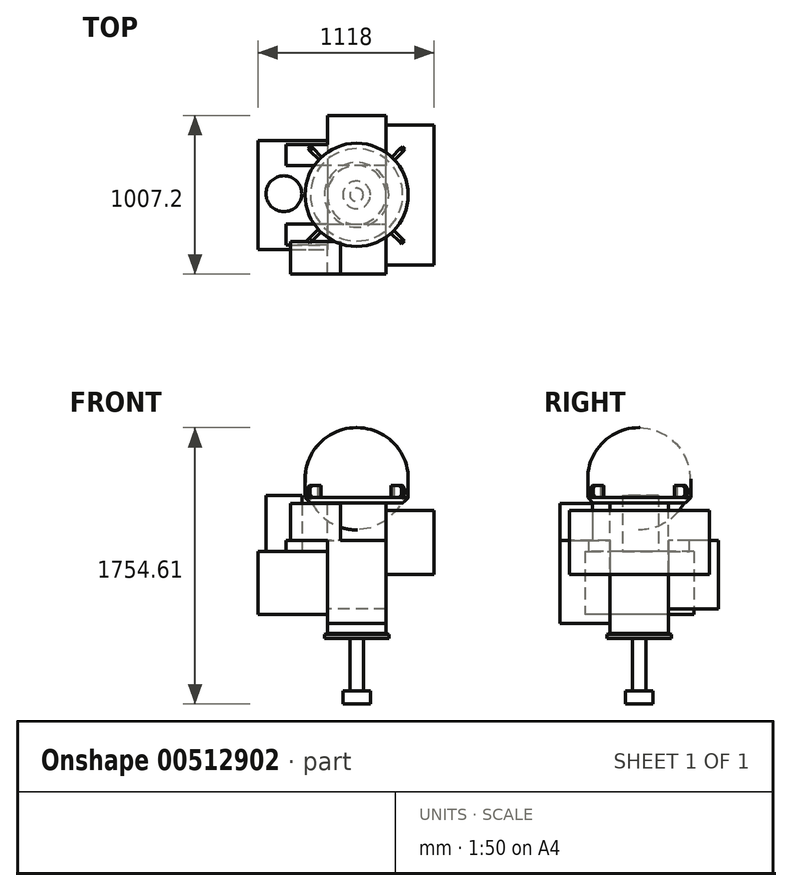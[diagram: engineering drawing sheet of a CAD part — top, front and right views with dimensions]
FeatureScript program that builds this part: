
annotation { "Feature Type Name" : "Feature", "Feature Type Description" : "" }
export const myFeature = defineFeature(function(context is Context, id is Id, definition is map)
    precondition{}
    {
        {
            var Q0;
            Q0=qCreatedBy(makeId("Front.planeOp"),FACE);
            var sketch = newSketch(context, id + "F0", { "sketchPlane" : qUnion([Q0])});
            skLineSegment(sketch, "E0", {"start": v(0, 0) * mm, "end": v(0, 25.3) * mm});
            skLineSegment(sketch, "E1", {"start": v(0, 25.3) * mm, "end": v(-18.9, 29.6) * mm});
            skLineSegment(sketch, "E2", {"start": v(-18.9, 29.6) * mm, "end": v(-18.9, 858.7) * mm});
            skLineSegment(sketch, "E3", {"start": v(-18.9, 858.7) * mm, "end": v(122.8, 858.7) * mm});
            skLineSegment(sketch, "E4", {"start": v(122.8, 858.7) * mm, "end": v(122.8, 1013) * mm});
            skLineSegment(sketch, "E5", {"start": v(-205, 1405.57) * mm, "end": v(-205, 307.85) * mm, "construction": true});
            skLineSegment(sketch, "E6", {"start": v(0, 0) * mm, "end": v(-205, 0) * mm});
            skPoint(sketch, "E7", {"position": v(-205, 1338) * mm});
            skArc(sketch, "E8", {"start": v(122.8, 1013) * mm, "mid": v(26.62, 1243.8) * mm, "end": v(-205, 1338) * mm});
            skLineSegment(sketch, "E9", {"start": v(-205, 1338) * mm, "end": v(-205, 0) * mm});
            skSolve(sketch);
        }
        {
            var Q0;
            Q0=makeQuery(id+"F0.imprint","IMPRINT",FACE,{"disambiguationData":[TD([[makeQuery(id+"F0.imprint","IMPRINT",EDGE,{"derivedFrom":sQuery(id+"F0.wireOp",EDGE,"E0")}),1.0]])]});
            var Q1;
            Q1=sQuery(id+"F0.wireOp",EDGE,"E5");
            revolve(context, id + "F1", {"entities" : qUnion([Q0]), "axis" : qUnion([Q1]), "revolveType" : RevolveType.FULL});
        }
        {
            var Q0;
            Q0=makeQuery(id+"F1.opRevolve","SWEPT_EDGE",EDGE,{"disambiguationData":[OSD([sQuery(id+"F0.wireOp",EDGE,"E3"),sQuery(id+"F0.wireOp",EDGE,"E4")])]});
            chamfer(context, id + "F2", {"entities" : qUnion([Q0]), "width" : 35 * mm, "tangentPropagation" : true});
        }
        {
            var Q0;
            Q0=makeQuery(id+"F1.opRevolve","SWEPT_EDGE",EDGE,{"disambiguationData":[OSD([sQuery(id+"F0.wireOp",EDGE,"E2"),sQuery(id+"F0.wireOp",EDGE,"E3")])]});
            fillet(context, id + "F3", {"entities" : qUnion([Q0]), "radius" : 8 * mm, "tangentPropagation" : true, "allowEdgeOverflow" : false});
        }
        {
            var Q0;
            Q0=makeQuery(id+"F1.opRevolve","SWEPT_FACE",FACE,{"disambiguationData":[OSD([sQuery(id+"F0.wireOp",EDGE,"E6")])]});
            var sketch = newSketch(context, id + "F4", { "sketchPlane" : qUnion([Q0])});
            skCircle(sketch, "E10", {"center": v(-205, 0) * mm, "radius": 42.3 * mm});
            skSolve(sketch);
        }
        {
            var Q0;
            Q0=makeQuery(id+"F4.imprint","IMPRINT",FACE,{"disambiguationData":[TD([[makeQuery(id+"F4.imprint","IMPRINT",EDGE,{"derivedFrom":sQuery(id+"F4.wireOp",EDGE,"E10")}),1.0]])]});
            extrude(context, id + "F5", {"entities" : qUnion([Q0]), "operationType" : NewBodyOperationType.ADD, "depth" : 416.6 * mm});
        }
        {
            var Q0;
            Q0=qCreatedBy(makeId("Right.planeOp"),FACE);
            cPlane(context, id + "F6", {"entities" : qUnion([Q0]), "cplaneType" : CPlaneType.OFFSET, "offset" : 18.9 * mm, "oppositeDirection" : true, "width" : 150 * mm, "height" : 150 * mm});
        }
        {
            var Q0;
            Q0=qCreatedBy(id+"F6.planeOp",FACE);
            var sketch = newSketch(context, id + "F7", { "sketchPlane" : qUnion([Q0])});
            skLineSegment(sketch, "E11.bottom", {"start": v(-445, 811.6) * mm, "end": v(445, 811.6) * mm});
            skLineSegment(sketch, "E11.top", {"start": v(-445, 405.8) * mm, "end": v(445, 405.8) * mm});
            skLineSegment(sketch, "E11.left", {"start": v(-445, 811.6) * mm, "end": v(-445, 405.8) * mm});
            skLineSegment(sketch, "E11.right", {"start": v(445, 811.6) * mm, "end": v(445, 405.8) * mm});
            skSolve(sketch);
        }
        {
            var Q0;
            Q0=qSketchRegion(id+"F7",true);
            extrude(context, id + "F8", {"entities" : qUnion([Q0]), "operationType" : NewBodyOperationType.ADD, "depth" : 305.8 * mm});
        }
        {
            var Q0;
            Q0=qCreatedBy(id+"F6.planeOp",FACE);
            cPlane(context, id + "F9", {"entities" : qUnion([Q0]), "cplaneType" : CPlaneType.OFFSET, "offset" : 372.2 * mm, "oppositeDirection" : true, "width" : 150 * mm, "height" : 150 * mm});
        }
        {
            var Q0;
            Q0=qCreatedBy(id+"F9.planeOp",FACE);
            var sketch = newSketch(context, id + "F10", { "sketchPlane" : qUnion([Q0])});
            skLineSegment(sketch, "E12.bottom", {"start": v(346, 552.3) * mm, "end": v(-346, 552.3) * mm});
            skLineSegment(sketch, "E12.top", {"start": v(346, 150.6) * mm, "end": v(-346, 150.6) * mm});
            skLineSegment(sketch, "E12.left", {"start": v(346, 552.3) * mm, "end": v(346, 150.6) * mm});
            skLineSegment(sketch, "E12.right", {"start": v(-346, 552.3) * mm, "end": v(-346, 150.6) * mm});
            skSolve(sketch);
        }
        {
            var Q0;
            Q0=qSketchRegion(id+"F10",true);
            extrude(context, id + "F11", {"entities" : qUnion([Q0]), "operationType" : NewBodyOperationType.ADD, "oppositeDirection" : true, "depth" : 440 * mm});
        }
        {
            var Q0;
            Q0=makeQuery(id+"F11.opExtrude","SWEPT_FACE",FACE,{"disambiguationData":[OSD([sQuery(id+"F10.wireOp",EDGE,"E12.bottom")])]});
            var sketch = newSketch(context, id + "F12", { "sketchPlane" : qUnion([Q0])});
            skCircle(sketch, "E13", {"center": v(-667.1, 7.5) * mm, "radius": 114 * mm});
            skSolve(sketch);
        }
        {
            var Q0;
            Q0=qSketchRegion(id+"F12",true);
            extrude(context, id + "F13", {"entities" : qUnion([Q0]), "operationType" : NewBodyOperationType.ADD, "depth" : 356.5 * mm});
        }
        {
            var Q0;
            Q0=qCreatedBy(makeId("Front.planeOp"),FACE);
            cPlane(context, id + "F14", {"entities" : qUnion([Q0]), "cplaneType" : CPlaneType.OFFSET, "offset" : 186.1 * mm, "width" : 150 * mm, "height" : 150 * mm});
        }
        {
            var Q0;
            Q0=qCreatedBy(id+"F14.planeOp",FACE);
            var sketch = newSketch(context, id + "F15", { "sketchPlane" : qUnion([Q0])});
            skLineSegment(sketch, "E14.bottom", {"start": v(-391.1, 622.7) * mm, "end": v(-18.9, 622.7) * mm});
            skLineSegment(sketch, "E14.top", {"start": v(-391.1, 94.5) * mm, "end": v(-18.9, 94.5) * mm});
            skLineSegment(sketch, "E14.left", {"start": v(-391.1, 622.7) * mm, "end": v(-391.1, 94.5) * mm});
            skLineSegment(sketch, "E14.right", {"start": v(-18.9, 622.7) * mm, "end": v(-18.9, 94.5) * mm});
            skSolve(sketch);
        }
        {
            var Q0;
            Q0=qSketchRegion(id+"F15",true);
            extrude(context, id + "F16", {"entities" : qUnion([Q0]), "depth" : 317.5 * mm});
        }
        {
            var Q0;
            Q0=qCreatedBy(makeId("Front.planeOp"),FACE);
            cPlane(context, id + "F17", {"entities" : qUnion([Q0]), "cplaneType" : CPlaneType.OFFSET, "offset" : 186.1 * mm, "oppositeDirection" : true, "width" : 150 * mm, "height" : 150 * mm});
        }
        {
            var Q0;
            Q0=qCreatedBy(id+"F17.planeOp",FACE);
            var sketch = newSketch(context, id + "F18", { "sketchPlane" : qUnion([Q0])});
            skLineSegment(sketch, "E15.bottom", {"start": v(-18.9, 621) * mm, "end": v(-391.1, 621) * mm});
            skLineSegment(sketch, "E15.top", {"start": v(-18.9, 186.6) * mm, "end": v(-391.1, 186.6) * mm});
            skLineSegment(sketch, "E15.left", {"start": v(-18.9, 621) * mm, "end": v(-18.9, 186.6) * mm});
            skLineSegment(sketch, "E15.right", {"start": v(-391.1, 621) * mm, "end": v(-391.1, 186.6) * mm});
            skSolve(sketch);
        }
        {
            var Q0;
            Q0=qSketchRegion(id+"F18",true);
            extrude(context, id + "F19", {"entities" : qUnion([Q0]), "oppositeDirection" : true, "depth" : 317.5 * mm});
        }
        {
            var Q0;
            Q0=makeQuery(id+"F16.opExtrude","SWEPT_FACE",FACE,{"disambiguationData":[OSD([sQuery(id+"F15.wireOp",EDGE,"E14.bottom")])]});
            var sketch = newSketch(context, id + "F20", { "sketchPlane" : qUnion([Q0])});
            skLineSegment(sketch, "E16.bottom", {"start": v(-626, -297.6) * mm, "end": v(-308.5, -297.6) * mm});
            skLineSegment(sketch, "E16.top", {"start": v(-626, -503.6) * mm, "end": v(-308.5, -503.6) * mm});
            skLineSegment(sketch, "E16.left", {"start": v(-626, -297.6) * mm, "end": v(-626, -503.6) * mm});
            skLineSegment(sketch, "E16.right", {"start": v(-308.5, -297.6) * mm, "end": v(-308.5, -503.6) * mm});
            skSolve(sketch);
        }
        {
            var Q0;
            Q0=qSketchRegion(id+"F20",true);
            extrude(context, id + "F21", {"entities" : qUnion([Q0]), "depth" : 234 * mm});
        }
        {
            var Q0;
            Q0=makeQuery(id+"F19.opExtrude","SWEPT_FACE",FACE,{"disambiguationData":[OSD([sQuery(id+"F18.wireOp",EDGE,"E15.bottom")])]});
            var sketch = newSketch(context, id + "F22", { "sketchPlane" : qUnion([Q0])});
            skLineSegment(sketch, "E17.bottom", {"start": v(-652.9, 318.2) * mm, "end": v(-391.1, 318.2) * mm});
            skLineSegment(sketch, "E17.top", {"start": v(-652.9, 186.1) * mm, "end": v(-391.1, 186.1) * mm});
            skLineSegment(sketch, "E17.left", {"start": v(-652.9, 318.2) * mm, "end": v(-652.9, 186.1) * mm});
            skLineSegment(sketch, "E17.right", {"start": v(-391.1, 318.2) * mm, "end": v(-391.1, 186.1) * mm});
            skSolve(sketch);
        }
        {
            var Q0;
            Q0=qSketchRegion(id+"F22",true);
            extrude(context, id + "F23", {"entities" : qUnion([Q0]), "operationType" : NewBodyOperationType.ADD, "endBound" : BoundingType.UP_TO_NEXT, "oppositeDirection" : true, "depth" : 25 * mm});
        }
        {
            var Q0;
            Q0=makeQuery(id+"F16.opExtrude","SWEPT_FACE",FACE,{"disambiguationData":[OSD([sQuery(id+"F15.wireOp",EDGE,"E14.bottom")])]});
            var sketch = newSketch(context, id + "F24", { "sketchPlane" : qUnion([Q0])});
            skLineSegment(sketch, "E18.bottom", {"start": v(-652.9, -186.1) * mm, "end": v(-391.1, -186.1) * mm});
            skLineSegment(sketch, "E18.top", {"start": v(-652.9, -318.2) * mm, "end": v(-391.1, -318.2) * mm});
            skLineSegment(sketch, "E18.left", {"start": v(-652.9, -186.1) * mm, "end": v(-652.9, -318.2) * mm});
            skLineSegment(sketch, "E18.right", {"start": v(-391.1, -186.1) * mm, "end": v(-391.1, -318.2) * mm});
            skSolve(sketch);
        }
        {
            var Q0;
            Q0=qSketchRegion(id+"F24",true);
            extrude(context, id + "F25", {"entities" : qUnion([Q0]), "operationType" : NewBodyOperationType.ADD, "endBound" : BoundingType.UP_TO_NEXT, "oppositeDirection" : true, "depth" : 25 * mm});
        }
        {
            var Q0;
            Q0=makeQuery(id+"F5.opExtrude","CAP_FACE",FACE,{"disambiguationData":[OSD([sQuery(id+"F4.wireOp",EDGE,"E10")])],"isStart":false});
            var sketch = newSketch(context, id + "F26", { "sketchPlane" : qUnion([Q0])});
            skCircle(sketch, "E19", {"center": v(-205, 0) * mm, "radius": 87.5 * mm});
            skSolve(sketch);
        }
        {
            var Q0;
            Q0 = qSketchRegion(id + "F26", true);
            extrude(context, id + "F27", {"entities" : qUnion([Q0]), "operationType" : NewBodyOperationType.ADD, "oppositeDirection" : true, "depth" : 83 * mm});
        }
        {
            var Q0;
            Q0=makeQuery(id+"F1.opRevolve","SWEPT_FACE",FACE,{"disambiguationData":[OSD([sQuery(id+"F0.wireOp",EDGE,"E3")])]});
            cPlane(context, id + "F28", {"entities" : qUnion([Q0]), "cplaneType" : CPlaneType.OFFSET, "offset" : 35 * mm, "oppositeDirection" : true, "width" : 150 * mm, "height" : 150 * mm});
        }
        {
            var Q0;
            Q0=qCreatedBy(id+"F28.planeOp",FACE);
            var sketch = newSketch(context, id + "F29", { "sketchPlane" : qUnion([Q0])});
            skLineSegment(sketch, "E20.bottom", {"start": v(-217.5, -425) * mm, "end": v(-192.5, -425) * mm});
            skLineSegment(sketch, "E20.top", {"start": v(-217.5, -325) * mm, "end": v(-192.5, -325) * mm});
            skLineSegment(sketch, "E20.left", {"start": v(-217.5, -425) * mm, "end": v(-217.5, -325) * mm});
            skLineSegment(sketch, "E20.right", {"start": v(-192.5, -425) * mm, "end": v(-192.5, -325) * mm});
            skLineSegment(sketch, "E21.1.0", {"start": v(85.8, -307.24) * mm, "end": v(15.1, -236.53) * mm});
            skLineSegment(sketch, "E21.1.1", {"start": v(85.8, -307.24) * mm, "end": v(103.48, -289.56) * mm});
            skLineSegment(sketch, "E21.1.2", {"start": v(103.48, -289.56) * mm, "end": v(32.77, -218.85) * mm});
            skLineSegment(sketch, "E21.1.3", {"start": v(15.1, -236.53) * mm, "end": v(32.77, -218.85) * mm});
            skLineSegment(sketch, "E21.2.0", {"start": v(217, -9.5) * mm, "end": v(117, -9.5) * mm});
            skLineSegment(sketch, "E21.2.1", {"start": v(217, -9.5) * mm, "end": v(217, 15.5) * mm});
            skLineSegment(sketch, "E21.2.2", {"start": v(217, 15.5) * mm, "end": v(117, 15.5) * mm});
            skLineSegment(sketch, "E21.2.3", {"start": v(117, -9.5) * mm, "end": v(117, 15.5) * mm});
            skLineSegment(sketch, "E21.3.0", {"start": v(99.24, 293.8) * mm, "end": v(28.53, 223.1) * mm});
            skLineSegment(sketch, "E21.3.1", {"start": v(99.24, 293.8) * mm, "end": v(81.56, 311.48) * mm});
            skLineSegment(sketch, "E21.3.2", {"start": v(81.56, 311.48) * mm, "end": v(10.85, 240.77) * mm});
            skLineSegment(sketch, "E21.3.3", {"start": v(28.53, 223.1) * mm, "end": v(10.85, 240.77) * mm});
            skLineSegment(sketch, "E21.4.0", {"start": v(-198.5, 425) * mm, "end": v(-198.5, 325) * mm});
            skLineSegment(sketch, "E21.4.1", {"start": v(-198.5, 425) * mm, "end": v(-223.5, 425) * mm});
            skLineSegment(sketch, "E21.4.2", {"start": v(-223.5, 425) * mm, "end": v(-223.5, 325) * mm});
            skLineSegment(sketch, "E21.4.3", {"start": v(-198.5, 325) * mm, "end": v(-223.5, 325) * mm});
            skLineSegment(sketch, "E21.5.0", {"start": v(-501.8, 307.24) * mm, "end": v(-431.1, 236.53) * mm});
            skLineSegment(sketch, "E21.5.1", {"start": v(-501.8, 307.24) * mm, "end": v(-519.48, 289.56) * mm});
            skLineSegment(sketch, "E21.5.2", {"start": v(-519.48, 289.56) * mm, "end": v(-448.77, 218.85) * mm});
            skLineSegment(sketch, "E21.5.3", {"start": v(-431.1, 236.53) * mm, "end": v(-448.77, 218.85) * mm});
            skLineSegment(sketch, "E21.6.0", {"start": v(-633, 9.5) * mm, "end": v(-533, 9.5) * mm});
            skLineSegment(sketch, "E21.6.1", {"start": v(-633, 9.5) * mm, "end": v(-633, -15.5) * mm});
            skLineSegment(sketch, "E21.6.2", {"start": v(-633, -15.5) * mm, "end": v(-533, -15.5) * mm});
            skLineSegment(sketch, "E21.6.3", {"start": v(-533, 9.5) * mm, "end": v(-533, -15.5) * mm});
            skLineSegment(sketch, "E21.7.0", {"start": v(-515.24, -293.8) * mm, "end": v(-444.53, -223.1) * mm});
            skLineSegment(sketch, "E21.7.1", {"start": v(-515.24, -293.8) * mm, "end": v(-497.56, -311.48) * mm});
            skLineSegment(sketch, "E21.7.2", {"start": v(-497.56, -311.48) * mm, "end": v(-426.85, -240.77) * mm});
            skLineSegment(sketch, "E21.7.3", {"start": v(-444.53, -223.1) * mm, "end": v(-426.85, -240.77) * mm});
            skPoint(sketch, "E21.center", {"position": v(-208, 0) * mm});
            skSolve(sketch);
        }
        {
            var Q0;
            Q0=makeQuery(id+"F29.imprint","IMPRINT",FACE,{"disambiguationData":[TD([[makeQuery(id+"F29.imprint","IMPRINT",EDGE,{"derivedFrom":sQuery(id+"F29.wireOp",EDGE,"E21.3.0")}),-1.0]])]});
            var Q1;
            Q1=makeQuery(id+"F29.imprint","IMPRINT",FACE,{"disambiguationData":[TD([[makeQuery(id+"F29.imprint","IMPRINT",EDGE,{"derivedFrom":sQuery(id+"F29.wireOp",EDGE,"E21.5.0")}),-1.0]])]});
            var Q2;
            Q2=makeQuery(id+"F29.imprint","IMPRINT",FACE,{"disambiguationData":[TD([[makeQuery(id+"F29.imprint","IMPRINT",EDGE,{"derivedFrom":sQuery(id+"F29.wireOp",EDGE,"E21.1.0")}),-1.0]])]});
            var Q3;
            Q3=makeQuery(id+"F29.imprint","IMPRINT",FACE,{"disambiguationData":[TD([[makeQuery(id+"F29.imprint","IMPRINT",EDGE,{"derivedFrom":sQuery(id+"F29.wireOp",EDGE,"E21.7.0")}),-1.0]])]});
            extrude(context, id + "F30", {"entities" : qUnion([Q0, Q1, Q2, Q3]), "operationType" : NewBodyOperationType.ADD, "oppositeDirection" : true, "depth" : 78 * mm});
        }
        {
            var Q0;
            Q0=makeQuery(id+"F30.opExtrude","CAP_EDGE",EDGE,{"disambiguationData":[OSD([sQuery(id+"F29.wireOp",EDGE,"E21.3.1")])],"isStart":false});
            var Q1;
            Q1=makeQuery(id+"F30.opExtrude","CAP_EDGE",EDGE,{"disambiguationData":[OSD([sQuery(id+"F29.wireOp",EDGE,"E21.3.1")])],"isStart":true});
            var Q2;
            Q2=makeQuery(id+"F30.opExtrude","CAP_EDGE",EDGE,{"disambiguationData":[OSD([sQuery(id+"F29.wireOp",EDGE,"E21.1.1")])],"isStart":false});
            var Q3;
            Q3=makeQuery(id+"F30.opExtrude","CAP_EDGE",EDGE,{"disambiguationData":[OSD([sQuery(id+"F29.wireOp",EDGE,"E21.1.1")])],"isStart":true});
            var Q4;
            Q4=makeQuery(id+"F30.opExtrude","CAP_EDGE",EDGE,{"disambiguationData":[OSD([sQuery(id+"F29.wireOp",EDGE,"E21.7.1")])],"isStart":false});
            var Q5;
            Q5=makeQuery(id+"F30.opExtrude","CAP_EDGE",EDGE,{"disambiguationData":[OSD([sQuery(id+"F29.wireOp",EDGE,"E21.7.1")])],"isStart":true});
            var Q6;
            Q6=makeQuery(id+"F30.opExtrude","CAP_EDGE",EDGE,{"disambiguationData":[OSD([sQuery(id+"F29.wireOp",EDGE,"E21.5.1")])],"isStart":false});
            var Q7;
            Q7=makeQuery(id+"F30.opExtrude","CAP_EDGE",EDGE,{"disambiguationData":[OSD([sQuery(id+"F29.wireOp",EDGE,"E21.5.1")])],"isStart":true});
            chamfer(context, id + "F31", {"entities" : qUnion([Q0, Q1, Q2, Q3, Q4, Q5, Q6, Q7]), "width" : 20 * mm, "tangentPropagation" : true});
        }
    });
